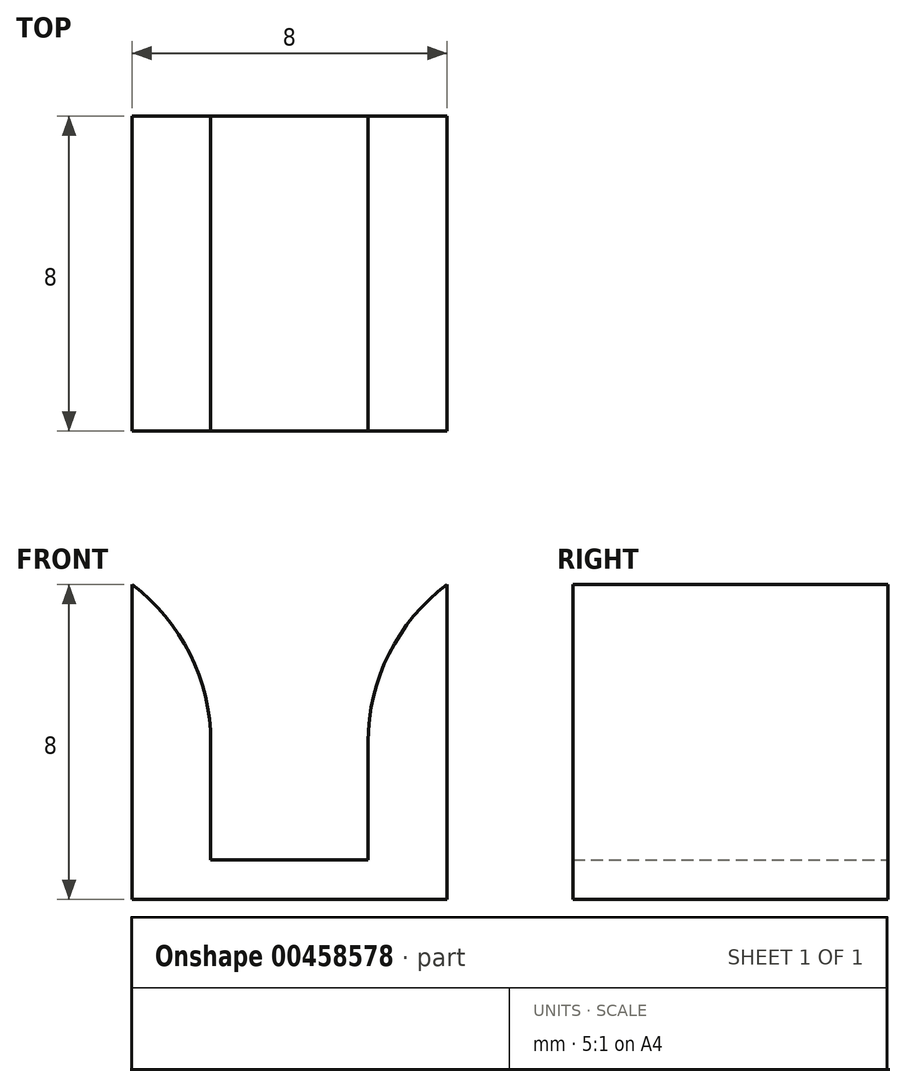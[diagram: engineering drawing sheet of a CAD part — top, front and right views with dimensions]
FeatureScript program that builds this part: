
annotation { "Feature Type Name" : "Feature", "Feature Type Description" : "" }
export const myFeature = defineFeature(function(context is Context, id is Id, definition is map)
    precondition{}
    {
        {
            var Q0;
            Q0=qCreatedBy(makeId("Front.planeOp"),FACE);
            var sketch = newSketch(context, id + "F0", { "sketchPlane" : qUnion([Q0])});
            skLineSegment(sketch, "E0.bottom", {"start": v(-4, 0.5) * mm, "end": v(4, 0.5) * mm});
            skLineSegment(sketch, "E0.top", {"start": v(-4, -0.5) * mm, "end": v(4, -0.5) * mm});
            skLineSegment(sketch, "E0.left", {"start": v(-4, 0.5) * mm, "end": v(-4, -0.5) * mm});
            skLineSegment(sketch, "E0.right", {"start": v(4, 0.5) * mm, "end": v(4, -0.5) * mm});
            skPoint(sketch, "E0.middle", {"position": v(0, 0) * mm});
            skLineSegment(sketch, "E1.bottom", {"start": v(-4, 0.5) * mm, "end": v(-2, 0.5) * mm});
            skLineSegment(sketch, "E1.top", {"start": v(-4, 7.5) * mm, "end": v(-2, 7.5) * mm});
            skLineSegment(sketch, "E1.left", {"start": v(-4, 0.5) * mm, "end": v(-4, 7.5) * mm});
            skLineSegment(sketch, "E1.right", {"start": v(-2, 0.5) * mm, "end": v(-2, 7.5) * mm});
            skLineSegment(sketch, "E2.bottom", {"start": v(4, 0.5) * mm, "end": v(2, 0.5) * mm});
            skLineSegment(sketch, "E2.top", {"start": v(4, 7.5) * mm, "end": v(2, 7.5) * mm});
            skLineSegment(sketch, "E2.left", {"start": v(4, 0.5) * mm, "end": v(4, 7.5) * mm});
            skLineSegment(sketch, "E2.right", {"start": v(2, 0.5) * mm, "end": v(2, 7.5) * mm});
            skSolve(sketch);
        }
        {
            var Q0;
            Q0 = qSketchRegion(id + "F0", true);
            extrude(context, id + "F1", {"entities" : qUnion([Q0]), "depth" : 8 * mm, "offsetDistance" : 25 * mm});
        }
        {
            var Q0;
            Q0=makeQuery(id+"F1.opExtrude","SWEPT_EDGE",EDGE,{"disambiguationData":[OSD([sQuery(id+"F0.wireOp",EDGE,"E1.top"),sQuery(id+"F0.wireOp",EDGE,"E1.right")])]});
            var Q1;
            Q1=makeQuery(id+"F1.opExtrude","SWEPT_EDGE",EDGE,{"disambiguationData":[OSD([sQuery(id+"F0.wireOp",EDGE,"E2.top"),sQuery(id+"F0.wireOp",EDGE,"E2.right")])]});
            fillet(context, id + "F2", {"entities" : qUnion([Q0, Q1]), "radius" : 5 * mm, "tangentPropagation" : true, "allowEdgeOverflow" : false});
        }
    });
